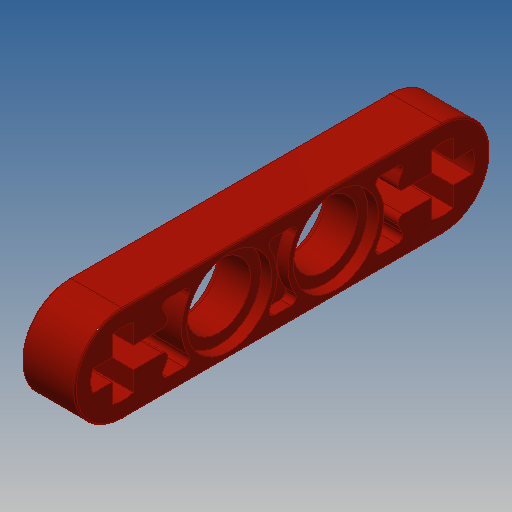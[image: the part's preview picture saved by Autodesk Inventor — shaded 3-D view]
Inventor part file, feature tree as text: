
AUTODESK INVENTOR PART (.ipt)
format: ipt  version: 2022.2 (Build 262287000, 287)  size: 276,480 bytes
history: native  units: mm
features: extrude x3, sketch x2, mirror x1, fillet x1
ambient origin geometry x8: Origin, YZ Plane, XZ Plane, XY Plane, X Axis, Y Axis, Z Axis, Center Point
bodies: Solid1 (feature_tree)
feature tree (7):
  extrude  "Extrusion4"  Depth=7.2mm
  sketch  "Sketch11"  dims[d53=1.6mm d56=0.1mm d58=24.0mm d59=6.4mm d60=4.8mm d61=6.4mm d62=0.8mm d63=0.0mm d64=45.0deg d65=0.8mm d66=0.0mm d67=0.4mm]
  extrude  "Extrusion16"  Depth=0.1mm
  extrude  "Extrusion17"  Depth=24.0mm
  mirror  "Mirror3"
  fillet  "Fillet1"  Radius=6.4mm
  sketch  "Sketch3"  dims[d15=4.0mm d16=0.0mm d47=4.8mm d49=7.2mm]
